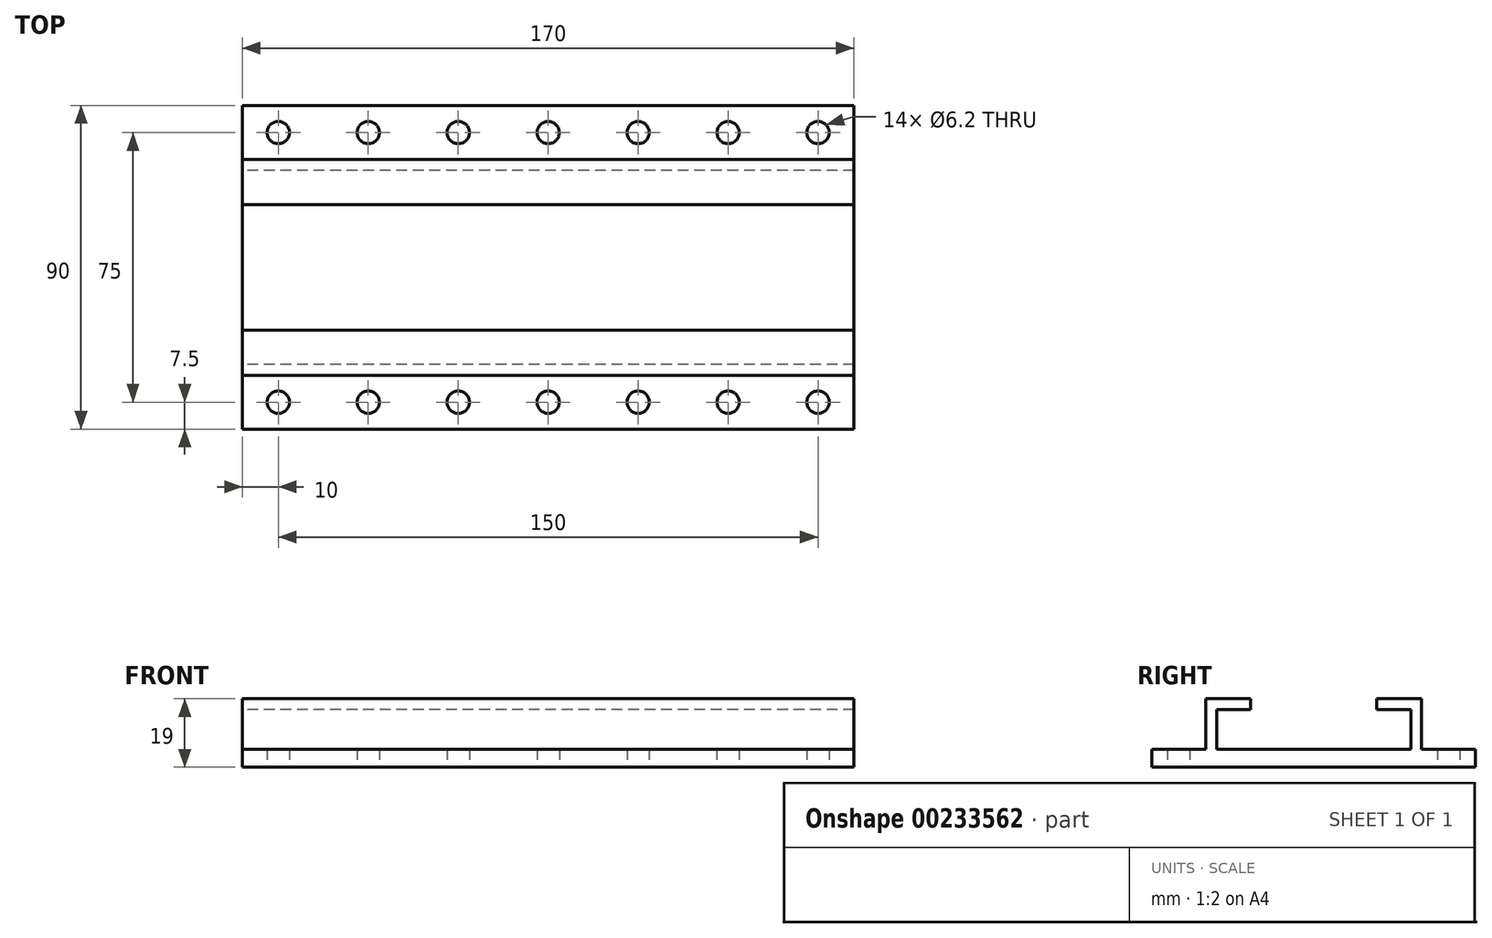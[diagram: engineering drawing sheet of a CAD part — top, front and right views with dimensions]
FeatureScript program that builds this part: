
annotation { "Feature Type Name" : "Feature", "Feature Type Description" : "" }
export const myFeature = defineFeature(function(context is Context, id is Id, definition is map)
    precondition{}
    {
        {
            var Q0;
            Q0=qCreatedBy(makeId("Right.planeOp"),FACE);
            var sketch = newSketch(context, id + "F0", { "sketchPlane" : qUnion([Q0])});
            skLineSegment(sketch, "E0.bottom", {"start": v(-45, 2.5) * mm, "end": v(45, 2.5) * mm});
            skLineSegment(sketch, "E0.top", {"start": v(-45, -2.5) * mm, "end": v(45, -2.5) * mm});
            skLineSegment(sketch, "E0.left", {"start": v(-45, 2.5) * mm, "end": v(-45, -2.5) * mm});
            skLineSegment(sketch, "E0.right", {"start": v(45, 2.5) * mm, "end": v(45, -2.5) * mm});
            skPoint(sketch, "E0.middle", {"position": v(0, 0) * mm});
            skLineSegment(sketch, "E1.bottom", {"start": v(-30, 2.5) * mm, "end": v(-27, 2.5) * mm});
            skLineSegment(sketch, "E1.top", {"start": v(-30, 13.5) * mm, "end": v(-27, 13.5) * mm});
            skLineSegment(sketch, "E1.left", {"start": v(-30, 2.5) * mm, "end": v(-30, 13.5) * mm});
            skLineSegment(sketch, "E1.right", {"start": v(-27, 2.5) * mm, "end": v(-27, 13.5) * mm});
            skLineSegment(sketch, "E2.bottom", {"start": v(-30, 13.5) * mm, "end": v(-17.5, 13.5) * mm});
            skLineSegment(sketch, "E2.top", {"start": v(-30, 16.5) * mm, "end": v(-17.5, 16.5) * mm});
            skLineSegment(sketch, "E2.left", {"start": v(-30, 13.5) * mm, "end": v(-30, 16.5) * mm});
            skLineSegment(sketch, "E2.right", {"start": v(-17.5, 13.5) * mm, "end": v(-17.5, 16.5) * mm});
            skLineSegment(sketch, "E3.MirrorCS", {"start": v(30, 13.5) * mm, "end": v(27, 13.5) * mm});
            skLineSegment(sketch, "E4.MirrorCS", {"start": v(30, 2.5) * mm, "end": v(27, 2.5) * mm});
            skLineSegment(sketch, "E5.MirrorCS", {"start": v(30, 2.5) * mm, "end": v(30, 13.5) * mm});
            skLineSegment(sketch, "E6.MirrorCS", {"start": v(30, 13.5) * mm, "end": v(30, 16.5) * mm});
            skLineSegment(sketch, "E7.MirrorCS", {"start": v(30, 13.5) * mm, "end": v(17.5, 13.5) * mm});
            skLineSegment(sketch, "E8.MirrorCS", {"start": v(27, 2.5) * mm, "end": v(27, 13.5) * mm});
            skLineSegment(sketch, "E9.MirrorCS", {"start": v(17.5, 13.5) * mm, "end": v(17.5, 16.5) * mm});
            skLineSegment(sketch, "E10.MirrorCS", {"start": v(30, 16.5) * mm, "end": v(17.5, 16.5) * mm});
            skSolve(sketch);
        }
        {
            var Q0;
            Q0 = qSketchRegion(id + "F0", true);
            extrude(context, id + "F1", {"entities" : qUnion([Q0]), "endBound" : BoundingType.SYMMETRIC, "depth" : 170 * mm});
        }
        {
            var Q0;
            Q0=makeQuery(id+"F1.opExtrude","SWEPT_FACE",FACE,{"disambiguationData":[OSD([sQuery(id+"F0.wireOp",EDGE,"E0.top")])]});
            var sketch = newSketch(context, id + "F2", { "sketchPlane" : qUnion([Q0])});
            skCircle(sketch, "E11", {"center": v(-75, 37.5) * mm, "radius": 3.1 * mm});
            skCircle(sketch, "E12", {"center": v(-50, 37.5) * mm, "radius": 3.1 * mm});
            skCircle(sketch, "E13", {"center": v(-25, 37.5) * mm, "radius": 3.1 * mm});
            skCircle(sketch, "E14", {"center": v(0, 37.5) * mm, "radius": 3.1 * mm});
            skPoint(sketch, "E15.MirrorP", {"position": v(25, 37.5) * mm});
            skCircle(sketch, "E16.MirrorC", {"center": v(25, 37.5) * mm, "radius": 3.1 * mm});
            skPoint(sketch, "E17.MirrorP", {"position": v(75, 37.5) * mm});
            skPoint(sketch, "E18.MirrorP", {"position": v(50, 37.5) * mm});
            skCircle(sketch, "E19.MirrorC", {"center": v(75, 37.5) * mm, "radius": 3.1 * mm});
            skCircle(sketch, "E20.MirrorC", {"center": v(50, 37.5) * mm, "radius": 3.1 * mm});
            skPoint(sketch, "E21.MirrorP", {"position": v(-25, -37.5) * mm});
            skCircle(sketch, "E22.MirrorC", {"center": v(50, -37.5) * mm, "radius": 3.1 * mm});
            skPoint(sketch, "E23.MirrorP", {"position": v(-50, -37.5) * mm});
            skCircle(sketch, "E24.MirrorC", {"center": v(75, -37.5) * mm, "radius": 3.1 * mm});
            skPoint(sketch, "E25.MirrorP", {"position": v(-75, -37.5) * mm});
            skCircle(sketch, "E26.MirrorC", {"center": v(25, -37.5) * mm, "radius": 3.1 * mm});
            skCircle(sketch, "E27.MirrorC", {"center": v(0, -37.5) * mm, "radius": 3.1 * mm});
            skCircle(sketch, "E28.MirrorC", {"center": v(-25, -37.5) * mm, "radius": 3.1 * mm});
            skCircle(sketch, "E29.MirrorC", {"center": v(-50, -37.5) * mm, "radius": 3.1 * mm});
            skCircle(sketch, "E30.MirrorC", {"center": v(-75, -37.5) * mm, "radius": 3.1 * mm});
            skSolve(sketch);
        }
        {
            var Q0;
            Q0 = qSketchRegion(id + "F2", true);
            extrude(context, id + "F3", {"entities" : qUnion([Q0]), "operationType" : NewBodyOperationType.REMOVE, "oppositeDirection" : true, "depth" : 6 * mm});
        }
    });
